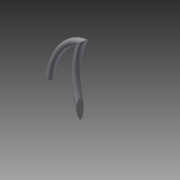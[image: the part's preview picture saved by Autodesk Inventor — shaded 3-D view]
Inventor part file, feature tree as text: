
AUTODESK INVENTOR PART (.ipt)
format: ipt  version: 2015 (Build 190159000, 159)  size: 152,576 bytes
history: native  units: in
note: dims shown in document units (in); Inventor stores cm internally (conversion verified against a paired STEP export)
features: sketch x3, plane x1, sweep x1, other x1
ambient origin geometry x8: Origin, YZ Plane, XZ Plane, XY Plane, X Axis, Y Axis, Z Axis, Center Point
bodies: Solid1 (feature_tree)
feature tree (6):
  sketch  "Sketch3"  dims[d0=0.4in d1=0.4in]
  sketch  "Sketch4"  dims[d2=0.404in]
  plane  "Work Plane1"
  sweep  "Sweep1"
  other  "Image1"
  sketch  "Sketch5"  dims[d3=0.1in d4=0.06in d5=0.06in d18=0.0in d19=0.0in]
